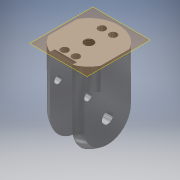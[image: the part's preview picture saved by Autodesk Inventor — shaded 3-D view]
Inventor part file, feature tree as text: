
AUTODESK INVENTOR PART (.ipt)
format: ipt  version: 2019 (Build 230136000, 136)  size: 167,424 bytes
history: native  units: in
note: dims shown in document units (in); Inventor stores cm internally (conversion verified against a paired STEP export)
features: reference x10, other x4, hole x2, sketch x2, projected_geometry x1
ambient origin geometry x8: Origin, YZ Plane, XZ Plane, XY Plane, X Axis, Y Axis, Z Axis, Center Point
bodies: Solid1 (feature_tree), Body (feature_tree)
feature tree (19):
  other  "plaszczyzna otwory"
  hole  "Otwór1"  [1 undecoded]
  hole  "Otwór2"  [1 undecoded]
  sketch  "Szkic1"
  reference  "Odniesienie1"
  projected_geometry  "Pętla rzutowana1"
  reference  "Odniesienie2"
  reference  "Odniesienie3"
  reference  "Odniesienie4"
  reference  "Odniesienie5"
  reference  "Odniesienie6"
  reference  "Odniesienie7"
  reference  "Odniesienie8"
  reference  "Odniesienie9"
  reference  "Odniesienie10"
  sketch  "Szkic2"
  other  "<userpath>\Downloads\reka\Finger all pieces assembled v10.iam"
  other  "Finger all pieces assembled v10.iam"
  other  "Base:1"
note: 2 required parameter values undecoded (feature->parameter linkage not recoverable at this tier; creation-order binding heuristic only, values carry confidence <= 0.55)
